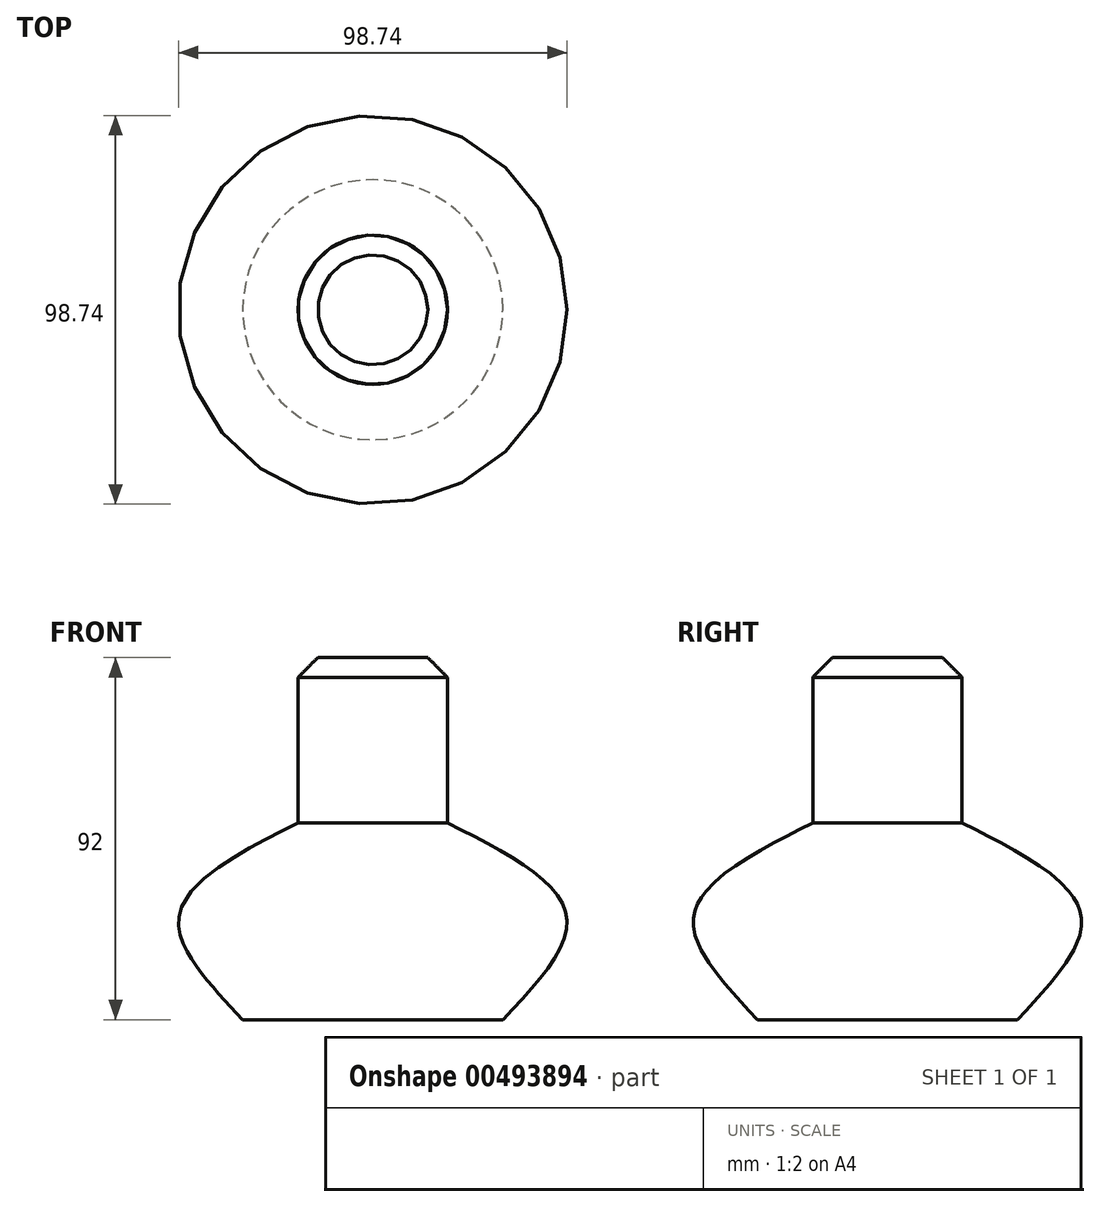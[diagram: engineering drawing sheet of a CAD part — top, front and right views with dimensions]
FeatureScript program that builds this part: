
annotation { "Feature Type Name" : "Feature", "Feature Type Description" : "" }
export const myFeature = defineFeature(function(context is Context, id is Id, definition is map)
    precondition{}
    {
        {
            var Q0;
            Q0=qCreatedBy(makeId("Top.planeOp"),FACE);
            cPlane(context, id + "F0", {"entities" : qUnion([Q0]), "cplaneType" : CPlaneType.OFFSET, "offset" : 25 * mm, "width" : 150 * mm, "height" : 150 * mm});
        }
        {
            var Q0;
            Q0=qCreatedBy(id+"F0.planeOp",FACE);
            cPlane(context, id + "F1", {"entities" : qUnion([Q0]), "cplaneType" : CPlaneType.OFFSET, "offset" : 25 * mm, "width" : 150 * mm, "height" : 150 * mm});
        }
        {
            var Q0;
            Q0=qCreatedBy(makeId("Top.planeOp"),FACE);
            var sketch = newSketch(context, id + "F2", { "sketchPlane" : qUnion([Q0])});
            skCircle(sketch, "E0", {"center": v(0, 0) * mm, "radius": 33.04 * mm});
            skSolve(sketch);
        }
        {
            var Q0;
            Q0=qCreatedBy(id+"F0.planeOp",FACE);
            var sketch = newSketch(context, id + "F3", { "sketchPlane" : qUnion([Q0])});
            skCircle(sketch, "E1", {"center": v(0, 0) * mm, "radius": 49.36 * mm});
            skSolve(sketch);
        }
        {
            var Q0;
            Q0=qCreatedBy(id+"F1.planeOp",FACE);
            var sketch = newSketch(context, id + "F4", { "sketchPlane" : qUnion([Q0])});
            skCircle(sketch, "E2", {"center": v(0, 0) * mm, "radius": 18.97 * mm});
            skSolve(sketch);
        }
        {
            var Q0;
            Q0=makeQuery(id+"F2.imprint","IMPRINT",FACE,{"disambiguationData":[TD([[makeQuery(id+"F2.imprint","IMPRINT",EDGE,{"derivedFrom":sQuery(id+"F2.wireOp",EDGE,"E0")}),1.0]])]});
            var Q1;
            Q1=makeQuery(id+"F3.imprint","IMPRINT",FACE,{"disambiguationData":[TD([[makeQuery(id+"F3.imprint","IMPRINT",EDGE,{"derivedFrom":sQuery(id+"F3.wireOp",EDGE,"E1")}),1.0]])]});
            var Q2;
            Q2=makeQuery(id+"F4.imprint","IMPRINT",FACE,{"disambiguationData":[TD([[makeQuery(id+"F4.imprint","IMPRINT",EDGE,{"derivedFrom":sQuery(id+"F4.wireOp",EDGE,"E2")}),1.0]])]});
            loft(context, id + "F5", {"sheetProfilesArray" : [{ "sheetProfileEntities" : qUnion([Q0]) }, { "sheetProfileEntities" : qUnion([Q1]) }, { "sheetProfileEntities" : qUnion([Q2]) }]});
        }
        {
            var Q0;
            Q0=makeQuery(id+"F5.opLoft","CAP_FACE",FACE,{"disambiguationData":[OSD([makeQuery(id+"F4.imprint","IMPRINT",FACE,{"disambiguationData":[TD([[makeQuery(id+"F4.imprint","IMPRINT",EDGE,{"derivedFrom":sQuery(id+"F4.wireOp",EDGE,"E2")}),1.0]])]})])],"isStart":true});
            extrude(context, id + "F6", {"entities" : qUnion([Q0]), "operationType" : NewBodyOperationType.ADD, "depth" : 42 * mm});
        }
        {
            var Q0;
            Q0=makeQuery(id+"F6.opExtrude","CAP_EDGE",EDGE,{"disambiguationData":[OSD([sQuery(id+"F2.wireOp",EDGE,"E0"),sQuery(id+"F4.wireOp",EDGE,"E2")])],"isStart":false});
            chamfer(context, id + "F7", {"entities" : qUnion([Q0]), "width" : 5 * mm, "tangentPropagation" : true});
        }
    });
